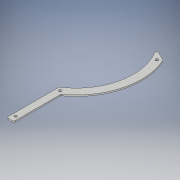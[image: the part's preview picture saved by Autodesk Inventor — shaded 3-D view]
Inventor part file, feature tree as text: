
AUTODESK INVENTOR PART (.ipt)
format: ipt  version: 2017 (Build 210142000, 142)  size: 140,288 bytes
history: native  units: in
note: dims shown in document units (in); Inventor stores cm internally (conversion verified against a paired STEP export)
features: sketch x2, extrude x1, hole x1
ambient origin geometry x8: Origin, YZ Plane, XZ Plane, XY Plane, X Axis, Y Axis, Z Axis, Center Point
bodies: Solid1 (feature_tree)
feature tree (4):
  extrude  "Extrusion1"  Depth=5.2in
  hole  "Hole1"  [1 undecoded]
  sketch  "Sketch1"  dims[d1=5.2in d2=0.2272in]
  sketch  "Sketch2"  dims[d3=0.5978in d4=11.9in d5=1.152in d6=4.75in d8=0.125in d9=0.125in d10=0.125in d11=0.125in d12=0.0in d13=11.15in d14=0.25in d15=0.25in d16=0.25in d17=0.5in d19=0.25in d20=0.75in d21=0.375in d22=0.25in d23=0.5635in d24=1.0in d25=0.8108in]
note: 1 required parameter value undecoded (feature->parameter linkage not recoverable at this tier; creation-order binding heuristic only, values carry confidence <= 0.55)
